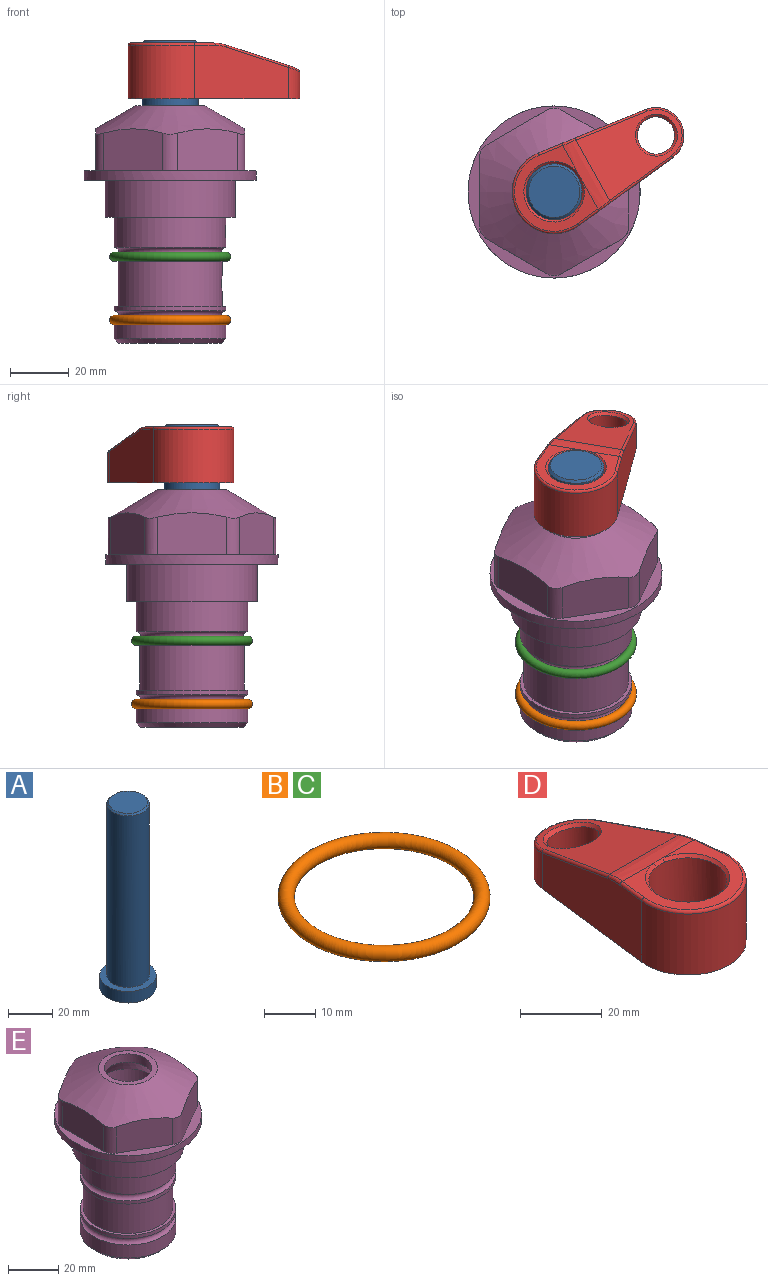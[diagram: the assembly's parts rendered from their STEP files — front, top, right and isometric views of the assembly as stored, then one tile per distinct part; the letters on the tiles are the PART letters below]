
ASSEMBLY  parts=5 mates=4
PART A: 6 faces, bbox 25.4x25.4x101.6 mm
  f0: plane 17.46x17.46mm, normal (0,0,1), area 239.5mm2, adj f5
  f1: plane 25.4x25.4mm, normal (0,0,-1), area 506.7mm2, adj f2
  f2: cylinder r=12.7mm len=25.4mm, axis (0,0,1), area 506.7mm2, adj f1,f3
  f3: plane 25.4x25.4mm, normal (0,0,1), area 221.7mm2, adj f2,f4
  f4: cylinder r=9.53mm len=94.46mm, axis (0,0,1), area 5653mm2, adj f3,f5
  f5: cone r=8.73mm half-angle=45deg, axis (0,0,-1), area 64.4mm2, adj f0,f4
PART B: 1 faces, bbox 44.7x44.7x3.2 mm
  f0: torus R=19.05mm, axis (0,0,1), area 1193.9mm2
PART C: same geometry as B
PART D: 31 faces, bbox 31.7x65.5x19.8 mm
  f0: plane 39.12x18.26mm, normal (0.99,0.12,0), area 612.2mm2, adj f1,f4,f7,f11,f13,f15
  f1: cylinder r=9.53mm len=18.91mm, axis (0,0,-1), area 296.1mm2, adj f0,f2,f7,f17
  f2: plane 39.12x18.26mm, normal (-0.99,0.12,0), area 612.2mm2, adj f1,f4,f7,f12,f14,f16
  f3: cylinder r=6.35mm len=12.7mm, axis (0,0,-1), area 362.4mm2, adj f7,f18
  f4: cylinder r=14.29mm len=28.58mm, axis (0,0,-1), area 882.2mm2, adj f0,f2,f7,f10
  f5: cylinder r=9.53mm len=19.05mm, axis (0,0,-1), area 1092.6mm2, adj f7,f19,f20
  f6: plane 26.99x23.69mm, normal (0,0,1), area 216.2mm2, adj f9,f10,f11,f12,f19
  f7: plane 63.5x28.58mm, normal (0,0,-1), area 661.8mm2, adj f0,f1,f2,f3,f4,f5,f22,f23
  f8: plane 33.52x23.6mm, normal (0,0.26,0.97), area 486mm2, adj f9,f15,f16,f17,f18
  f9: cylinder r=19.05mm len=24.72mm, axis (1,0,0), area 120.4mm2, adj f6,f8,f13,f14,f20
  f10: torus R=13.49mm, axis (0,0,1), area 59mm2, adj f4,f6,f11,f12
  f11: cylinder r=0.79mm len=8.67mm, axis (0.12,-0.99,0), area 10.8mm2, adj f0,f6,f10,f13
  f12: cylinder r=0.79mm len=8.67mm, axis (0.12,0.99,0), area 10.8mm2, adj f2,f6,f10,f14
  f13: bspline ~4.95x1.42mm, area 6.1mm2, adj f0,f9,f11,f15
  f14: bspline ~4.95x1.42mm, area 6.1mm2, adj f2,f9,f12,f16
  f15: cylinder r=0.79mm len=25.95mm, axis (0.12,-0.96,0.26), area 32.9mm2, adj f0,f8,f13,f17
  f16: cylinder r=0.79mm len=25.95mm, axis (0.12,0.96,-0.26), area 32.9mm2, adj f2,f8,f14,f17
  f17: bspline ~18.91x8.38mm, area 30mm2, adj f1,f8,f15,f16
  f18: bspline ~14.29x14.29mm, area 48.3mm2, adj f3,f8
  f19: cone r=9.53mm half-angle=45deg, axis (0,0,1), area 66.5mm2, adj f5,f6,f20
  f20: bspline ~3.22x0.96mm, area 3.5mm2, adj f5,f9,f19
  f21: plane 2.75x2.72mm, normal (0,0,-1), area 2.9mm2, adj f23,f25,f28
  f22: plane 23.05x15.88mm, normal (-0.99,-0.12,0), area 323.6mm2, adj f7,f25,f26,f27,f28,f29
  f23: plane 23.05x15.88mm, normal (0.99,-0.12,0), area 323.6mm2, adj f7,f21,f25,f27,f28,f30
  f24: cylinder r=9.53mm len=10.69mm, axis (0,0,-1), area 114.7mm2, adj f7,f27,f29,f30
  f25: cylinder r=12.7mm len=20.59mm, axis (0,0,-1), area 381.1mm2, adj f7,f21,f22,f23,f26,f28
  f26: plane 2.75x2.72mm, normal (0,0,-1), area 2.9mm2, adj f22,f25,f28
  f27: plane 19.72x18.37mm, normal (0,-0.26,-0.97), area 291.8mm2, adj f22,f23,f24,f28,f29,f30
  f28: cylinder r=15.88mm len=19.92mm, axis (1,0,0), area 54.8mm2, adj f21,f22,f23,f25,f26,f27
  f29: cylinder r=1.59mm len=11mm, axis (0,0,-1), area 34.7mm2, adj f7,f22,f24,f27
  f30: cylinder r=1.59mm len=11mm, axis (0,0,-1), area 34.7mm2, adj f7,f23,f24,f27
PART E: 36 faces, bbox 58.7x58.7x81 mm
  f0: cylinder r=17.78mm len=35.56mm, axis (0,0,1), area 1670.8mm2, adj f23,f24,f31
  f1: cylinder r=19.05mm len=38.1mm, axis (0,0,1), area 1191.9mm2, adj f26,f27,f30
  f2: plane 58.66x58.66mm, normal (0,0,-1), area 1150.6mm2, adj f3,f28
  f3: cylinder r=29.33mm len=58.66mm, axis (0,0,-1), area 585.1mm2, adj f2,f4
  f4: plane 58.66x58.66mm, normal (0,0,1), area 475.9mm2, adj f3,f5,f6,f7,f8,f9,f10,f11
  f5: plane 20.32x14.34mm, normal (-0.5,0.87,0), area 324.4mm2, adj f4,f15,f16,f17
  f6: plane 20.32x14.34mm, normal (0.5,0.87,0), area 324.4mm2, adj f4,f14,f15,f17
  f7: plane 23.48x14.34mm, normal (1,0,0), area 324.4mm2, adj f4,f13,f14,f17
  f8: plane 20.32x14.34mm, normal (0.5,-0.87,0), area 324.4mm2, adj f4,f12,f13,f17
  f9: plane 20.32x14.34mm, normal (-0.5,-0.87,0), area 324.4mm2, adj f4,f11,f12,f17
  f10: plane 23.48x14.34mm, normal (-1,0,0), area 324.4mm2, adj f4,f11,f16,f17
  f11: cylinder r=5.08mm len=12.85mm, axis (0,0,-1), area 67.2mm2, adj f4,f9,f10,f17
  f12: cylinder r=5.08mm len=12.85mm, axis (0,0,-1), area 67.2mm2, adj f4,f8,f9,f17
  f13: cylinder r=5.08mm len=12.85mm, axis (0,0,-1), area 67.2mm2, adj f4,f7,f8,f17
  f14: cylinder r=5.08mm len=12.85mm, axis (0,0,-1), area 67.2mm2, adj f4,f6,f7,f17
  f15: cylinder r=5.08mm len=12.85mm, axis (0,0,-1), area 67.2mm2, adj f4,f5,f6,f17
  f16: cylinder r=5.08mm len=12.85mm, axis (0,0,-1), area 67.2mm2, adj f4,f5,f10,f17
  f17: cone r=11.73mm half-angle=60deg, axis (0,0,-1), area 2071.8mm2, adj f5,f6,f7,f8,f9,f10,f11,f12
  f18: plane 23.46x23.46mm, normal (0,0,1), area 147.4mm2, adj f17,f35
  f19: plane 34.93x34.93mm, normal (0,0,-1), area 958mm2, adj f29
  f20: cylinder r=19.05mm len=38.1mm, axis (0,0,1), area 760.1mm2, adj f21,f29
  f21: torus R=19.05mm, axis (0,0,1), area 565.3mm2, adj f20,f22
  f22: cylinder r=19.05mm len=38.1mm, axis (0,0,1), area 190mm2, adj f21,f23
  f23: plane 38.1x38.1mm, normal (0,0,1), area 146.9mm2, adj f0,f22
  f24: plane 38.1x38.1mm, normal (0,0,-1), area 146.9mm2, adj f0,f25
  f25: cylinder r=19.05mm len=38.1mm, axis (0,0,1), area 190mm2, adj f24,f26
  f26: torus R=19.05mm, axis (0,0,1), area 565.3mm2, adj f1,f25
  f27: plane 44.45x44.45mm, normal (0,0,-1), area 411.7mm2, adj f1,f28
  f28: cylinder r=22.23mm len=44.45mm, axis (0,0,1), area 1773.5mm2, adj f2,f27
  f29: cone r=19.05mm half-angle=45deg, axis (0,0,1), area 257.5mm2, adj f19,f20
  f30: cylinder r=3.17mm len=6.75mm, axis (-1,0,0), area 128mm2, adj f1,f33
  f31: cylinder r=3.17mm len=6.35mm, axis (-1,0,0), area 102.5mm2, adj f0,f33
  f32: plane 25.4x25.4mm, normal (0,0,1), area 506.7mm2, adj f33
  f33: cylinder r=12.7mm len=66.42mm, axis (0,0,-1), area 5236.2mm2, adj f30,f31,f32,f34
  f34: cone r=9.53mm half-angle=30deg, axis (0,0,-1), area 443.4mm2, adj f33,f35
  f35: cylinder r=9.53mm len=19.05mm, axis (0,0,-1), area 240.9mm2, adj f18,f34
PLACE A rot(axis=(0,0,-1),61deg) t=(0,0,-15.94)mm
PLACE B t=(0,0,-23.18)mm
PLACE C t=(0,0,-1.59)mm
PLACE D rot(axis=(0,0,-1),61deg) t=(0,0,-16.73)mm
PLACE E at identity fixed
MATE fastened C.f0 <-> E.f0  axis (0,0,1) through (0,0,-26.1)mm
MATE cylindrical A.f2 <-> E.f0  axis (0,0,-1) through (0,0,-54.04)mm
MATE fastened B.f0 <-> E.f0  axis (0,0,1) through (0,0,-47.69)mm
MATE fastened A.f2 <-> D.f4  axis (0,0,1) through (0,0,46.77)mm
